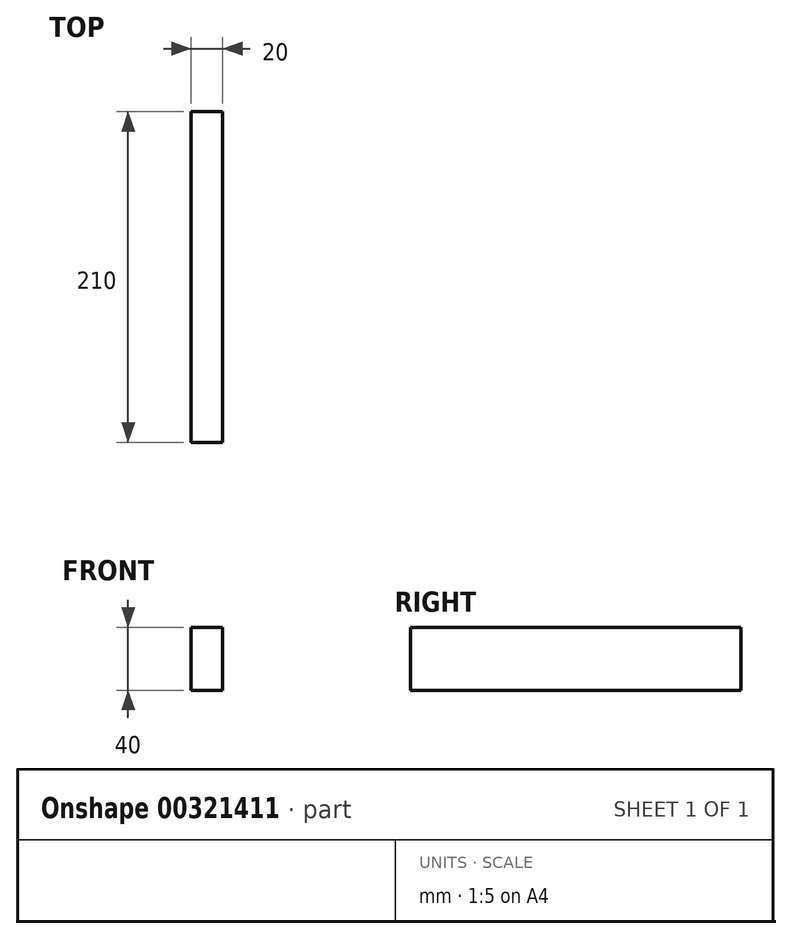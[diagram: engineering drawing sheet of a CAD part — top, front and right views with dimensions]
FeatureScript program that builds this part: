
annotation { "Feature Type Name" : "Feature", "Feature Type Description" : "" }
export const myFeature = defineFeature(function(context is Context, id is Id, definition is map)
    precondition{}
    {
        {
            var Q0;
            Q0=qCreatedBy(makeId("Front.planeOp"),FACE);
            var sketch = newSketch(context, id + "F0", { "sketchPlane" : qUnion([Q0])});
            skLineSegment(sketch, "E0.bottom", {"start": v(-10, 20) * mm, "end": v(10, 20) * mm});
            skLineSegment(sketch, "E0.top", {"start": v(-10, -20) * mm, "end": v(10, -20) * mm});
            skLineSegment(sketch, "E0.left", {"start": v(-10, 20) * mm, "end": v(-10, -20) * mm});
            skLineSegment(sketch, "E0.right", {"start": v(10, 20) * mm, "end": v(10, -20) * mm});
            skSolve(sketch);
        }
        {
            var Q0;
            Q0=makeQuery(id+"F0.imprint","IMPRINT",FACE,{"disambiguationData":[TD([[makeQuery(id+"F0.imprint","IMPRINT",EDGE,{"derivedFrom":sQuery(id+"F0.wireOp",EDGE,"E0.bottom")}),-1.0]])]});
            extrude(context, id + "F1", {"entities" : qUnion([Q0]), "depth" : 210 * mm});
        }
    });
